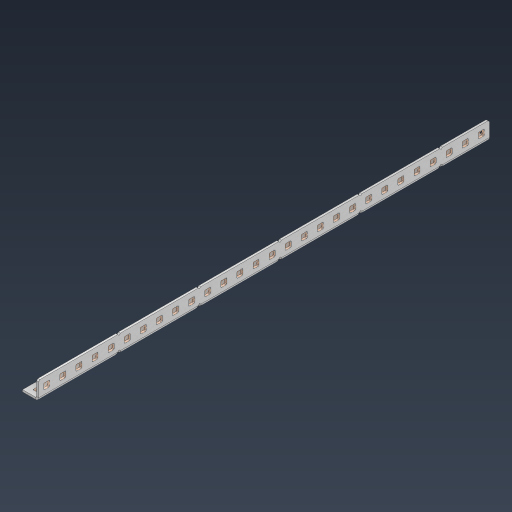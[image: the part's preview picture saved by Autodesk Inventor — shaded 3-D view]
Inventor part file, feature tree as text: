
AUTODESK INVENTOR PART (.ipt)
format: ipt  version: 2024.3 (Build 283343000, 343)  size: 1,072,128 bytes
history: native  units: in
note: dims shown in document units (in); Inventor stores cm internally (conversion verified against a paired STEP export)
features: other x91, extrude x82, sheet_metal_op x11, pattern_linear x2, mirror x1, chamfer x1, sketch x1
ambient origin geometry x8: Origin, YZ Plane, XZ Plane, XY Plane, X Axis, Y Axis, Z Axis, Center Point
bodies: Solid1 (feature_tree), Body (feature_tree)
feature tree (189):
  sheet_metal_op  "Flanges"
  other  "Flange Pattern Plane"
  other  "Flange Pattern Sketch"
  sheet_metal_op  "Flange Pattern"
  sheet_metal_op  "Body Pattern"
  pattern_linear  "Center Pattern"  Spacing1=14.0in  [1 undecoded]
  other  "Arc Length"
  mirror  "Notch Mirror"
  pattern_linear  "Notch Pattern"  Spacing1=0.0625in  [1 undecoded]
  chamfer  "End Chamfer"
  extrude  "Half Cut"  Depth=0.0625in
  other  "Plate1"
  sketch  "Sketch2"  dims[d0=1.0in d1=14.0in d2=0.0625in d3=0.0625in d4=0.0312in d5=0.125in d6=0.0625in d7=0.5in d8=90.0deg d9=0.0312in d10=0.25in d11=0.0625in d12=0.0625in d16=0.182in d17=0.02in d18=0.0625in d19=0.0in d20=0.25in d21=0.25in d38=11.0236in d40=0.5in d41=0.3937in d43=1.0in d46=0.172in d47=1.0in d48=0.0in d49=0.182in d50=0.02in d51=0.25in d52=0.25in d53=0.0625in d54=0.0in d55=0.172in d56=1.0in d57=0.0in d58=0.25in d60=11.0236in d62=0.5in d63=0.3937in d65=0.5in d85=0.1473in d86=0.1782in d88=0.04in d89=0.0625in d90=0.0in d91=0.04in d92=0.0491in d95=2.5in d96=0.04in d97=0.25in d98=45.0deg d99=0.25in d100=0.5in d101=0.0in d102=2.497in d106=0.182in d107=0.02in d108=0.5in d109=0.5in d110=0.0625in d111=0.0in d112=0.172in d113=0.5in d114=0.0in d117=0.5in d118=0.5in d119=0.5in]
  other  "Plate2"
  sheet_metal_op  "Bend1"
  sheet_metal_op  "Corner1"
  other  "Srf1"
  other  "Srf2"
  other  "Srf91"
  sheet_metal_op  "Body Pattern Sketch"
  other  "Srf92"
  other  "Srf786"
  other  "Srf823"
  other  "Srf824"
  other  "Srf825"
  other  "Srf826"
  other  "Srf827"
  other  "Srf828"
  other  "Srf829"
  other  "Srf856"
  other  "Srf857"
  other  "Srf858"
  other  "Srf859"
  other  "Srf860"
  other  "Srf861"
  other  "Srf862"
  other  "Srf889"
  other  "Srf890"
  other  "Srf891"
  other  "Srf892"
  other  "Srf893"
  other  "Srf894"
  other  "Srf895"
  other  "Srf896"
  other  "Srf922"
  other  "Srf923"
  other  "Srf924"
  other  "Srf925"
  other  "Srf926"
  other  "Srf959"
  other  "Srf960"
  other  "Srf961"
  other  "Srf962"
  other  "Srf963"
  other  "Srf996"
  other  "Srf997"
  other  "Srf998"
  other  "Srf999"
  other  "Srf1000"
  other  "Srf1143"
  other  "Srf1144"
  other  "Srf1145"
  other  "Srf1146"
  other  "Srf1147"
  other  "Srf1148"
  other  "Srf1149"
  other  "Srf1150"
  other  "Srf1151"
  other  "Srf1152"
  other  "Srf1153"
  other  "Srf1154"
  other  "Srf1155"
  other  "Srf1156"
  other  "Srf1199"
  other  "Srf1200"
  other  "Srf1201"
  other  "Srf1202"
  other  "Srf1203"
  other  "Srf1204"
  other  "Srf1205"
  other  "Srf1206"
  other  "Srf1207"
  other  "Srf1208"
  other  "Srf1209"
  other  "Srf1210"
  other  "Srf1211"
  other  "Srf1212"
  other  "Srf1255"
  other  "Srf1256"
  other  "Srf1257"
  other  "Srf1258"
  other  "Srf1259"
  other  "Srf1260"
  other  "Srf1261"
  other  "Srf1262"
  other  "Srf1263"
  other  "Srf1264"
  other  "Srf1265"
  other  "Srf1266"
  other  "Srf1267"
  other  "Srf1268"
  sheet_metal_op  "Flange Stamp"
  sheet_metal_op  "Flange Circle"
  sheet_metal_op  "Body Stamp"
  sheet_metal_op  "Body Circle"
  other  "Center Stamp"
  other  "Center Circle"
  sheet_metal_op  "Notch"
  extrude  "ExtrusionSrf2"  Depth=0.0312in
  extrude  "ExtrusionSrf92"  Depth=0.5in
  extrude  "ExtrusionSrf823"  Depth=0.0625in
  extrude  "ExtrusionSrf824"  Depth=0.5in TaperAngle=90.0deg
  extrude  "ExtrusionSrf825"  Depth=0.25in
  extrude  "ExtrusionSrf826"  Depth=0.0625in
  extrude  "ExtrusionSrf827"  Depth=0.0625in
  extrude  "ExtrusionSrf828"  Depth=0.182in
  extrude  "ExtrusionSrf829"  Depth=0.02in
  extrude  "ExtrusionSrf856"  Depth=0.0625in
  extrude  "ExtrusionSrf857"  TaperAngle=0.0deg  [1 undecoded]
  extrude  "ExtrusionSrf858"  Depth=0.25in
  extrude  "ExtrusionSrf859"  Depth=0.25in
  extrude  "ExtrusionSrf860"  Depth=0.5in
  extrude  "ExtrusionSrf861"  Depth=0.5in
  extrude  "ExtrusionSrf862"  Depth=1.0in TaperAngle=0.0deg
  extrude  "ExtrusionSrf889"  Depth=0.182in
  extrude  "ExtrusionSrf890"  Depth=0.02in
  extrude  "ExtrusionSrf891"  Depth=0.25in
  extrude  "ExtrusionSrf892"  Depth=0.25in
  extrude  "ExtrusionSrf893"  Depth=0.0625in
  extrude  "ExtrusionSrf894"  TaperAngle=0.0deg  [1 undecoded]
  extrude  "ExtrusionSrf895"  Depth=0.5in
  extrude  "ExtrusionSrf896"  Depth=1.0in TaperAngle=0.0deg
  extrude  "ExtrusionSrf922"  Depth=0.25in
  extrude  "ExtrusionSrf923"  Depth=0.5in
  extrude  "ExtrusionSrf924"  Depth=0.5in
  extrude  "ExtrusionSrf925"  Depth=0.5in
  extrude  "ExtrusionSrf926"  Depth=0.5in
  extrude  "ExtrusionSrf959"  Depth=0.5in
  extrude  "ExtrusionSrf960"  Depth=0.0625in
  extrude  "ExtrusionSrf961"  TaperAngle=0.0deg  [1 undecoded]
  extrude  "ExtrusionSrf962"  Depth=0.5in
  extrude  "ExtrusionSrf963"  Depth=0.5in
  extrude  "ExtrusionSrf996"  Depth=2.5in
  extrude  "ExtrusionSrf997"  Depth=0.25in TaperAngle=45.0deg
  extrude  "ExtrusionSrf998"  Depth=0.25in
  extrude  "ExtrusionSrf999"  Depth=0.5in TaperAngle=0.0deg
  extrude  "ExtrusionSrf1000"  Depth=0.5in
  extrude  "ExtrusionSrf1143"  Depth=0.182in
  extrude  "ExtrusionSrf1144"  Depth=0.02in
  extrude  "ExtrusionSrf1145"  Depth=0.5in
  extrude  "ExtrusionSrf1146"  Depth=0.5in
  extrude  "ExtrusionSrf1147"  Depth=0.0625in
  extrude  "ExtrusionSrf1148"  TaperAngle=0.0deg  [1 undecoded]
  extrude  "ExtrusionSrf1149"  Depth=0.5in
  extrude  "ExtrusionSrf1150"  Depth=0.5in TaperAngle=0.0deg
  extrude  "ExtrusionSrf1151"  Depth=0.5in
  extrude  "ExtrusionSrf1152"  Depth=0.5in
  extrude  "ExtrusionSrf1153"  Depth=0.5in
  extrude  "ExtrusionSrf1154"  [1 undecoded]
  extrude  "ExtrusionSrf1155"  [1 undecoded]
  extrude  "ExtrusionSrf1156"  [1 undecoded]
  extrude  "ExtrusionSrf1199"  [1 undecoded]
  extrude  "ExtrusionSrf1200"  [1 undecoded]
  extrude  "ExtrusionSrf1201"  [1 undecoded]
  extrude  "ExtrusionSrf1202"  [1 undecoded]
  extrude  "ExtrusionSrf1203"  [1 undecoded]
  extrude  "ExtrusionSrf1204"  [1 undecoded]
  extrude  "ExtrusionSrf1205"  [1 undecoded]
  extrude  "ExtrusionSrf1206"  [1 undecoded]
  extrude  "ExtrusionSrf1207"  [1 undecoded]
  extrude  "ExtrusionSrf1208"  [1 undecoded]
  extrude  "ExtrusionSrf1209"  [1 undecoded]
  extrude  "ExtrusionSrf1210"  [1 undecoded]
  extrude  "ExtrusionSrf1211"  [1 undecoded]
  extrude  "ExtrusionSrf1212"  [1 undecoded]
  extrude  "ExtrusionSrf1255"  [1 undecoded]
  extrude  "ExtrusionSrf1256"  [1 undecoded]
  extrude  "ExtrusionSrf1257"  [1 undecoded]
  extrude  "ExtrusionSrf1258"  [1 undecoded]
  extrude  "ExtrusionSrf1259"  [1 undecoded]
  extrude  "ExtrusionSrf1260"  [1 undecoded]
  extrude  "ExtrusionSrf1261"  [1 undecoded]
  extrude  "ExtrusionSrf1262"  [1 undecoded]
  extrude  "ExtrusionSrf1263"  [1 undecoded]
  extrude  "ExtrusionSrf1264"  [1 undecoded]
  extrude  "ExtrusionSrf1265"  [1 undecoded]
  extrude  "ExtrusionSrf1266"  [1 undecoded]
  extrude  "ExtrusionSrf1267"  [1 undecoded]
  extrude  "ExtrusionSrf1268"  [1 undecoded]
note: 37 required parameter values undecoded (feature->parameter linkage not recoverable at this tier; creation-order binding heuristic only, values carry confidence <= 0.55)
